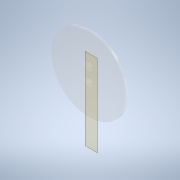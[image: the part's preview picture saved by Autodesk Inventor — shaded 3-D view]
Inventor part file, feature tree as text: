
AUTODESK INVENTOR PART (.ipt)
format: ipt  version: 2021 (Build 250183000, 183)  size: 159,232 bytes
history: native  units: mm
features: other x6, reference x4, extrude x2, chamfer x2, sketch x1
ambient origin geometry x8: Origin, YZ Plane, XZ Plane, XY Plane, X Axis, Y Axis, Z Axis, Center Point
bodies: Body1 (feature_tree)
feature tree (15):
  other  "Bryła1"
  other  "Płaszczyzna konstrukcyjna1"
  extrude  "Wyciągnięcie proste1"  Depth=7.5mm
  chamfer  "Faza1"  Distance=7.5mm
  chamfer  "Faza3"  Distance=80.0mm
  extrude  "Wyciągnięcie proste2"  Depth=3.0mm TaperAngle=0.0deg
  sketch  "Szkic1"
  reference  "Odniesienie1"
  reference  "Odniesienie2"
  reference  "Odniesienie3"
  reference  "Odniesienie4"
  parser-record x1  (decoder bookkeeping rows leaked as tree rows — omitted from the tree; the rows remain in map.json)
  other  "model tensometru.iam"
  other  "tensometr:1"
  other  "Zespół1"
note: 1 file-system path scrubbed to <path> (originals preserved in map.json)
